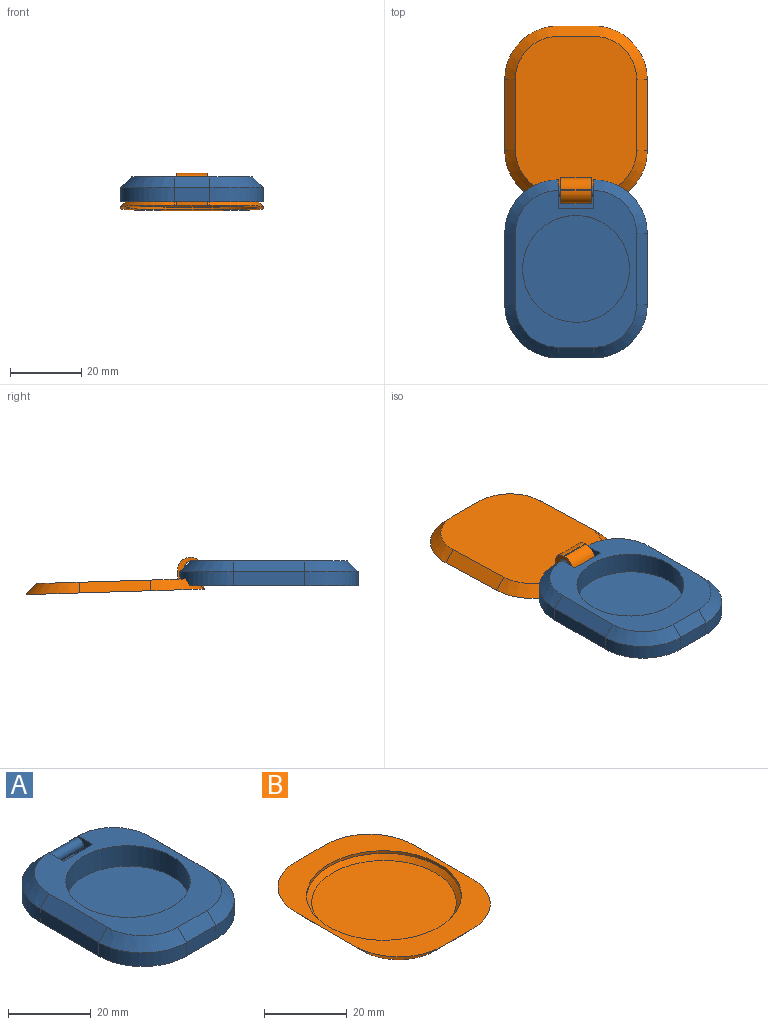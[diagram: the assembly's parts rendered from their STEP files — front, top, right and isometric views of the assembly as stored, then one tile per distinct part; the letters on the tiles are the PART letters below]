
ASSEMBLY  parts=2 mates=1
PART A: 24 faces, bbox 40x50x7 mm
  f0: plane 20x4mm, normal (1,0,0), area 80mm2, adj f1,f7,f9,f18
  f1: cylinder r=15mm len=15mm, axis (0,0,-1), area 94.2mm2, adj f0,f2,f9,f13,f17
  f2: plane 10x1mm, normal (0,1,0), area 10mm2, adj f1,f3,f9,f10
  f3: cylinder r=15mm len=15mm, axis (0,0,-1), area 94.2mm2, adj f2,f4,f9,f11,f23
  f4: plane 20x4mm, normal (-1,0,0), area 80mm2, adj f3,f5,f9,f22
  f5: cylinder r=15mm len=15mm, axis (0,0,-1), area 94.2mm2, adj f4,f6,f9,f21
  f6: plane 10x4mm, normal (0,-1,0), area 40mm2, adj f5,f7,f9,f20
  f7: cylinder r=15mm len=15mm, axis (0,0,-1), area 94.2mm2, adj f0,f6,f9,f19
  f8: plane 44x34mm, normal (0,0,1), area 615.5mm2, adj f11,f12,f13,f15,f17,f18,f19,f20
  f9: plane 50x40mm, normal (0,0,-1), area 1806.9mm2, adj f0,f1,f2,f3,f4,f5,f6,f7
  f10: plane 10x8mm, normal (0,0,1), area 80mm2, adj f2,f11,f12,f13
  f11: plane 8x6mm, normal (1,0,0), area 36.4mm2, adj f3,f8,f10,f12,f16,f23
  f12: plane 10x6mm, normal (0,1,0), area 60mm2, adj f8,f10,f11,f13
  f13: plane 8x6mm, normal (-1,0,0), area 36.4mm2, adj f1,f8,f10,f12,f16,f17
  f14: plane 30x30mm, normal (0,0,1), area 706.9mm2, adj f15
  f15: cylinder r=15mm len=30mm, axis (0,0,1), area 565.5mm2, adj f8,f14
  f16: cylinder r=1.5mm len=10mm, axis (1,0,0), area 94.2mm2, adj f11,f13
  f17: cone r=12mm half-angle=45deg, axis (0,0,-1), area 90mm2, adj f1,f8,f13,f18
  f18: plane 20x3mm, normal (0.71,0,0.71), area 84.9mm2, adj f0,f8,f17,f19
  f19: cone r=12mm half-angle=45deg, axis (0,0,-1), area 90mm2, adj f7,f8,f18,f20
  f20: plane 10x3mm, normal (0,-0.71,0.71), area 42.4mm2, adj f6,f8,f19,f21
  f21: cone r=12mm half-angle=45deg, axis (0,0,-1), area 90mm2, adj f5,f8,f20,f22
  f22: plane 20x3mm, normal (-0.71,0,0.71), area 84.9mm2, adj f4,f8,f21,f23
  f23: cone r=12mm half-angle=45deg, axis (0,0,-1), area 90mm2, adj f3,f8,f11,f22
PART B: 22 faces, bbox 40x50x9 mm
  f0: plane 20x3mm, normal (0.71,0,-0.71), area 84.9mm2, adj f2,f4,f13,f14
  f1: plane 20x3mm, normal (-0.71,0,-0.71), area 84.9mm2, adj f2,f4,f16,f17
  f2: plane 44x34mm, normal (0,0,-1), area 1336.3mm2, adj f0,f1,f6,f7,f8,f12,f13,f14
  f3: plane 8.5x5.5mm, normal (0,1,0), area 46.8mm2, adj f4,f6,f7,f10
  f4: plane 50x40mm, normal (0,0,1), area 708.3mm2, adj f0,f1,f3,f12,f13,f14,f15,f16
  f5: plane 8.5x0.25mm, normal (0,0,-1), area 2.1mm2, adj f6,f7,f10,f11
  f6: plane 9x7.25mm, normal (-1,0,0), area 30.2mm2, adj f2,f3,f5,f8,f9,f10,f11,f18
  f7: plane 9x7.25mm, normal (1,0,0), area 30.2mm2, adj f2,f3,f5,f8,f9,f10,f11,f12
  f8: plane 8.5x2.5mm, normal (0,-1,0), area 21.3mm2, adj f2,f6,f7,f11
  f9: cylinder r=2mm len=8.5mm, axis (1,0,0), area 106.8mm2, adj f6,f7
  f10: cylinder r=3.5mm len=8.5mm, axis (1,0,0), area 46.7mm2, adj f3,f5,f6,f7
  f11: cylinder r=3.5mm len=8.5mm, axis (1,0,0), area 46.7mm2, adj f5,f6,f7,f8
  f12: plane 3x3mm, normal (0,0.71,-0.71), area 3.2mm2, adj f2,f4,f7,f13
  f13: cone r=15mm half-angle=45deg, axis (0,0,1), area 90mm2, adj f0,f2,f4,f12
  f14: cone r=15mm half-angle=45deg, axis (0,0,1), area 90mm2, adj f0,f2,f4,f15
  f15: plane 10x3mm, normal (0,-0.71,-0.71), area 42.4mm2, adj f2,f4,f14,f16
  f16: cone r=15mm half-angle=45deg, axis (0,0,1), area 90mm2, adj f1,f2,f4,f15
  f17: cone r=15mm half-angle=45deg, axis (0,0,1), area 90mm2, adj f1,f2,f4,f18
  f18: plane 3x3mm, normal (0,0.71,-0.71), area 3.2mm2, adj f2,f4,f6,f17
  f19: plane 34.91x34.91mm, normal (0,0,1), area 957.4mm2, adj f21
  f20: cylinder r=18.7mm len=37.4mm, axis (0,0,1), area 89mm2, adj f4,f21
  f21: cone r=18.7mm half-angle=45deg, axis (0,0,1), area 199.6mm2, adj f19,f20
PLACE A at identity fixed
PLACE B rot(axis=(1,0,0),178.2deg) t=(0,43.54,9.32)mm
MATE revolute A.f16 <-> B.f9  axis (1,0,0) through (0,21.7,5)mm
